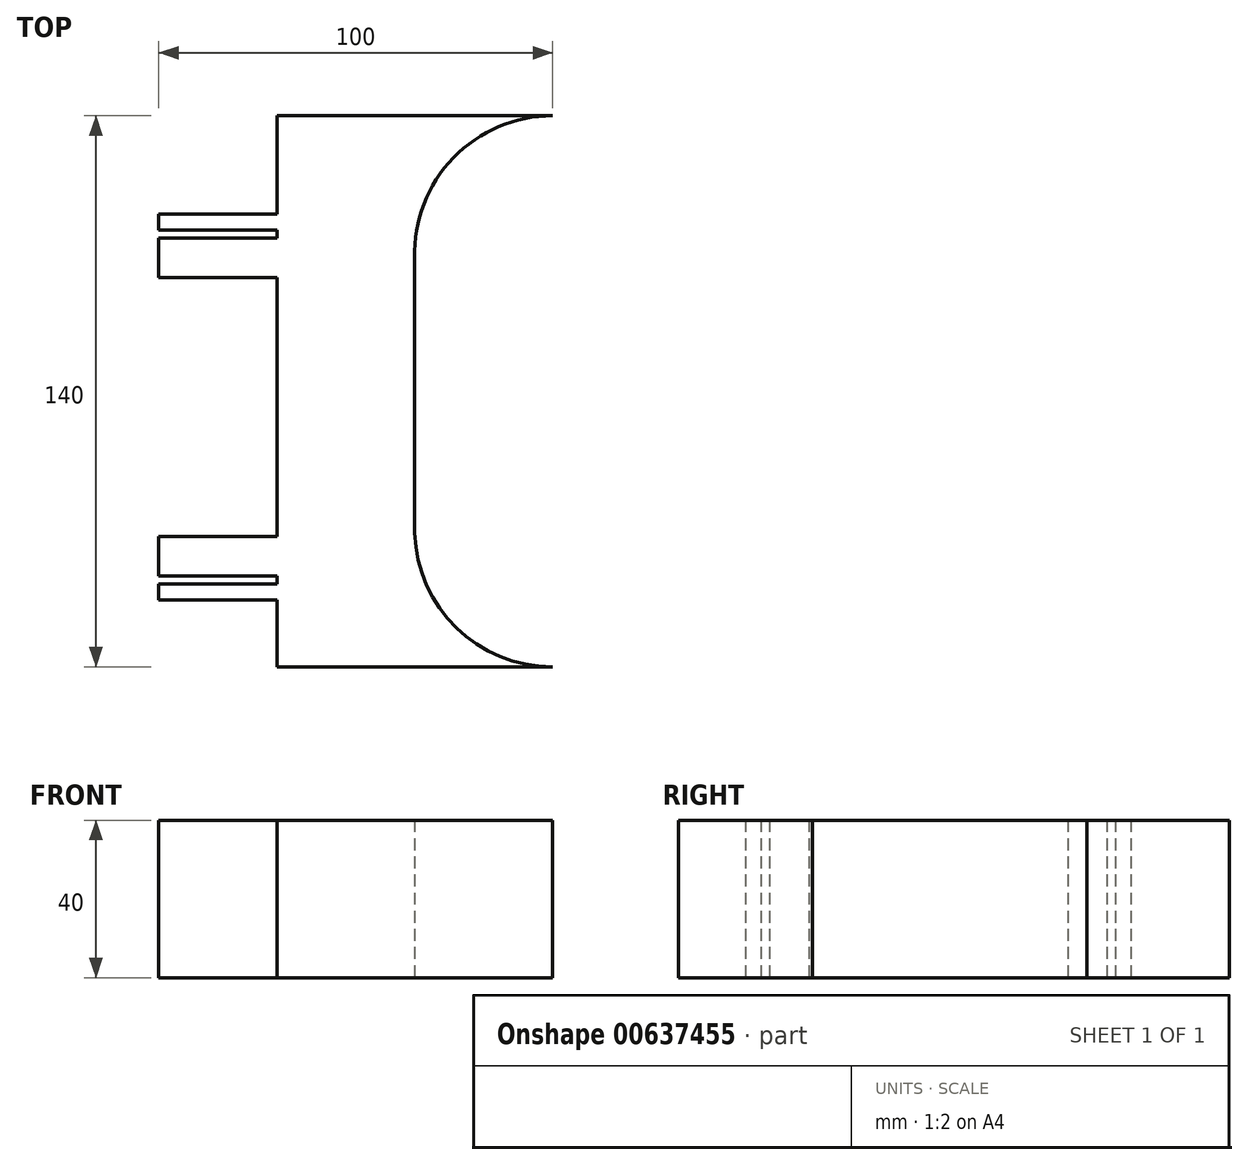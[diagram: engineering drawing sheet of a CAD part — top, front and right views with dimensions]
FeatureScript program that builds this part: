
annotation { "Feature Type Name" : "Feature", "Feature Type Description" : "" }
export const myFeature = defineFeature(function(context is Context, id is Id, definition is map)
    precondition{}
    {
        {
            var Q0;
            Q0=qCreatedBy(makeId("Top.planeOp"),FACE);
            var sketch = newSketch(context, id + "F0", { "sketchPlane" : qUnion([Q0])});
            skLineSegment(sketch, "E0.bottom", {"start": v(-35, -70) * mm, "end": v(35, -70) * mm});
            skLineSegment(sketch, "E0.top", {"start": v(-35, 70) * mm, "end": v(35, 70) * mm});
            skLineSegment(sketch, "E0.left", {"start": v(-35, -70) * mm, "end": v(-35, 70) * mm});
            skLineSegment(sketch, "E0.right", {"start": v(35, -70) * mm, "end": v(35, 70) * mm});
            skPoint(sketch, "E0.middle", {"position": v(0, 0) * mm});
            skLineSegment(sketch, "E1", {"start": v(35, 0) * mm, "end": v(-35, 0) * mm});
            skCircle(sketch, "E2", {"center": v(35, -35) * mm, "radius": 35 * mm});
            skLineSegment(sketch, "E3.MirrorCS", {"start": v(35, 70) * mm, "end": v(35, -70) * mm});
            skCircle(sketch, "E4.MirrorC", {"center": v(35, 35) * mm, "radius": 35 * mm});
            skLineSegment(sketch, "E5.bottom", {"start": v(-35, 45) * mm, "end": v(-65, 45) * mm});
            skLineSegment(sketch, "E5.top", {"start": v(-35, -53) * mm, "end": v(-65, -53) * mm});
            skLineSegment(sketch, "E5.left", {"start": v(-35, 45) * mm, "end": v(-35, -53) * mm});
            skLineSegment(sketch, "E5.right", {"start": v(-65, 45) * mm, "end": v(-65, -53) * mm});
            skLineSegment(sketch, "E6.bottom", {"start": v(-35, 41) * mm, "end": v(-65, 41) * mm});
            skLineSegment(sketch, "E6.top", {"start": v(-35, -49) * mm, "end": v(-65, -49) * mm});
            skLineSegment(sketch, "E6.left", {"start": v(-35, 41) * mm, "end": v(-35, -49) * mm});
            skLineSegment(sketch, "E6.right", {"start": v(-65, 41) * mm, "end": v(-65, -49) * mm});
            skLineSegment(sketch, "E7", {"start": v(-65, -46.9) * mm, "end": v(-35, -46.9) * mm});
            skLineSegment(sketch, "E8", {"start": v(-65, 38.9) * mm, "end": v(-35, 38.9) * mm});
            skLineSegment(sketch, "E9", {"start": v(-65, -36.9) * mm, "end": v(-35, -36.9) * mm});
            skLineSegment(sketch, "E10", {"start": v(-65, 28.9) * mm, "end": v(-35, 28.9) * mm});
            skSolve(sketch);
        }
        {
            var Q0;
            {var subQ0=sQuery(id+"F0.wireOp",EDGE,"E0.top");Q0=makeQuery(id+"F0.imprint","IMPRINT",FACE,{"disambiguationData":[TD([[makeQuery(id+"F0.imprint","IMPRINT",EDGE,{"derivedFrom":subQ0}),-1.0]])]});}
            var Q1;
            {var subQ0=sQuery(id+"F0.wireOp",EDGE,"E0.bottom");Q1=makeQuery(id+"F0.imprint","IMPRINT",FACE,{"disambiguationData":[TD([[makeQuery(id+"F0.imprint","IMPRINT",EDGE,{"derivedFrom":subQ0}),1.0]])]});}
            var Q2;
            {var subQ0=sQuery(id+"F0.wireOp",EDGE,"E8");Q2=makeQuery(id+"F0.imprint","IMPRINT",FACE,{"disambiguationData":[TD([[makeQuery(id+"F0.imprint","IMPRINT",EDGE,{"derivedFrom":subQ0}),-1.0]])]});}
            var Q3;
            {var subQ0=sQuery(id+"F0.wireOp",EDGE,"E5.bottom");Q3=makeQuery(id+"F0.imprint","IMPRINT",FACE,{"disambiguationData":[TD([[makeQuery(id+"F0.imprint","IMPRINT",EDGE,{"derivedFrom":subQ0}),1.0]])]});}
            var Q4;
            {var subQ0=sQuery(id+"F0.wireOp",EDGE,"E5.top");Q4=makeQuery(id+"F0.imprint","IMPRINT",FACE,{"disambiguationData":[TD([[makeQuery(id+"F0.imprint","IMPRINT",EDGE,{"derivedFrom":subQ0}),-1.0]])]});}
            var Q5;
            {var subQ0=sQuery(id+"F0.wireOp",EDGE,"E7");Q5=makeQuery(id+"F0.imprint","IMPRINT",FACE,{"disambiguationData":[TD([[makeQuery(id+"F0.imprint","IMPRINT",EDGE,{"derivedFrom":subQ0}),1.0]])]});}
            extrude(context, id + "F1", {"entities" : qUnion([Q0, Q1, Q2, Q3, Q4, Q5]), "depth" : 40 * mm, "offsetDistance" : 25 * mm});
        }
        {
            var Q0;
            Q0=qCreatedBy(makeId("Top.planeOp"),FACE);
            var sketch = newSketch(context, id + "F2", { "sketchPlane" : qUnion([Q0])});
            skLineSegment(sketch, "E11.bottom", {"start": v(0, -36) * mm, "end": v(38.36, -36) * mm});
            skLineSegment(sketch, "E11.top", {"start": v(0, 33.84) * mm, "end": v(38.36, 33.84) * mm});
            skLineSegment(sketch, "E11.left", {"start": v(0, -36) * mm, "end": v(0, 33.84) * mm});
            skLineSegment(sketch, "E11.right", {"start": v(38.36, -36) * mm, "end": v(38.36, 33.84) * mm});
            skSolve(sketch);
        }
        {
            var Q0;
            Q0=makeQuery(id+"F2.imprint","IMPRINT",FACE,{"disambiguationData":[TD([[makeQuery(id+"F2.imprint","IMPRINT",EDGE,{"derivedFrom":sQuery(id+"F2.wireOp",EDGE,"E11.bottom")}),1.0]])]});
            extrude(context, id + "F3", {"entities" : qUnion([Q0]), "operationType" : NewBodyOperationType.REMOVE, "depth" : 78.31 * mm, "offsetDistance" : 25 * mm});
        }
    });
